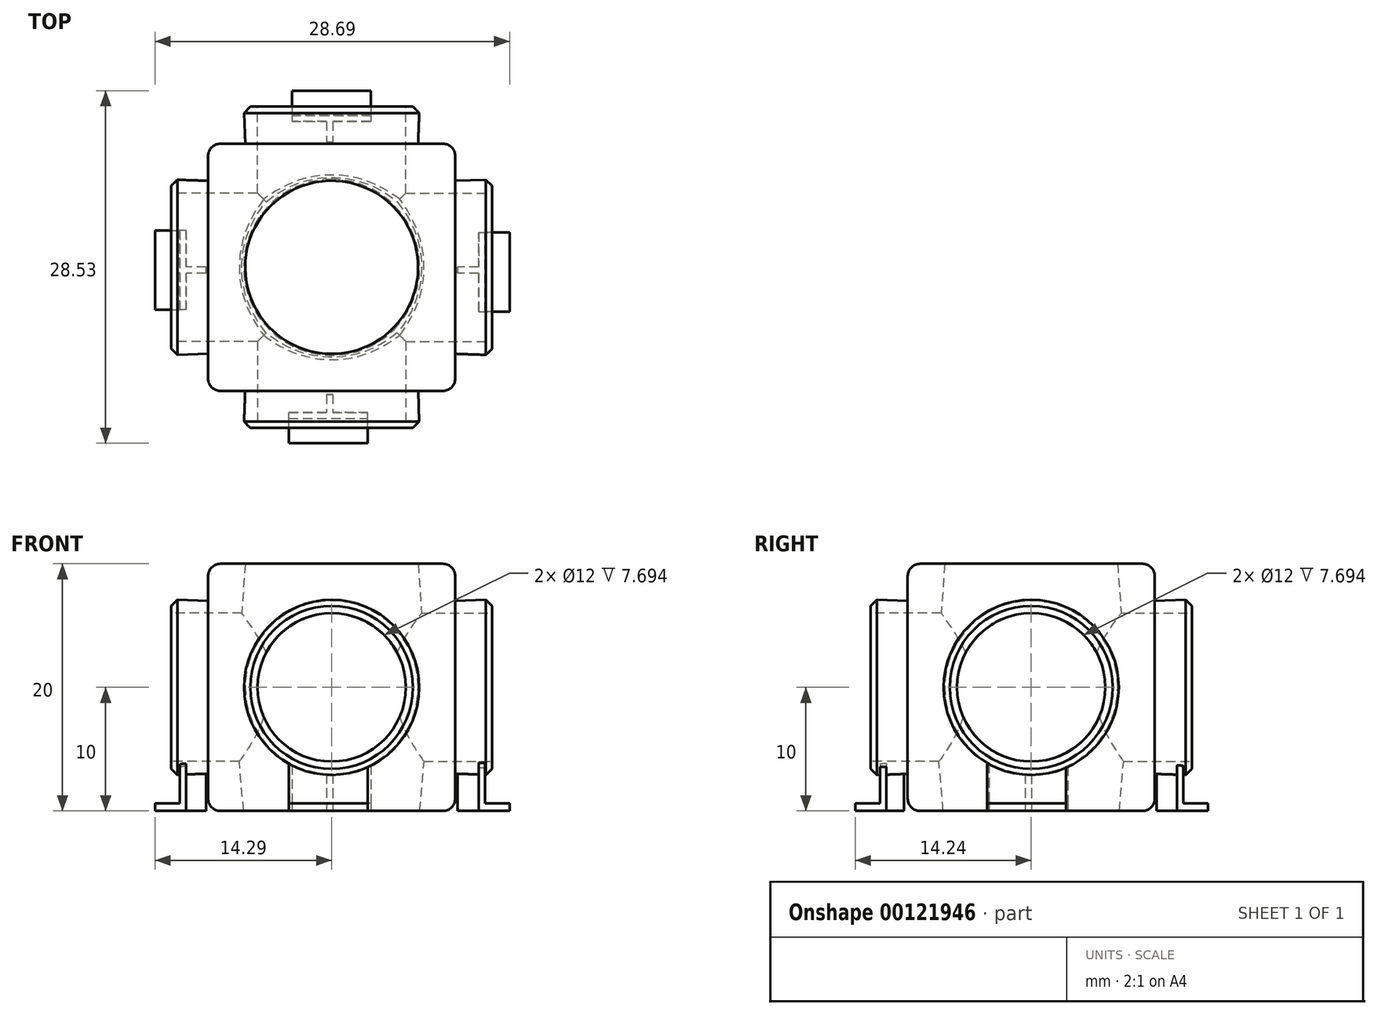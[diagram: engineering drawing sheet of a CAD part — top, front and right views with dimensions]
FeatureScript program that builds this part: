
annotation { "Feature Type Name" : "Feature", "Feature Type Description" : "" }
export const myFeature = defineFeature(function(context is Context, id is Id, definition is map)
    precondition{}
    {
        {
            var Q0;
            Q0=qCreatedBy(makeId("Top.planeOp"),FACE);
            var sketch = newSketch(context, id + "F0", { "sketchPlane" : qUnion([Q0])});
            skLineSegment(sketch, "E0.bottom", {"start": v(0, 0) * mm, "end": v(20, 0) * mm});
            skLineSegment(sketch, "E0.top", {"start": v(0, 20) * mm, "end": v(20, 20) * mm});
            skLineSegment(sketch, "E0.left", {"start": v(0, 0) * mm, "end": v(0, 20) * mm});
            skLineSegment(sketch, "E0.right", {"start": v(20, 0) * mm, "end": v(20, 20) * mm});
            skSolve(sketch);
        }
        {
            var Q0;
            Q0=makeQuery(id+"F0.imprint","IMPRINT",FACE,{"disambiguationData":[TD([[makeQuery(id+"F0.imprint","IMPRINT",EDGE,{"derivedFrom":sQuery(id+"F0.wireOp",EDGE,"E0.bottom")}),1.0]])]});
            extrude(context, id + "F1", {"entities" : qUnion([Q0]), "depth" : 20 * mm});
        }
        {
            var Q0;
            Q0=makeQuery(id+"F1.opExtrude","CAP_FACE",FACE,{"disambiguationData":[OSD([sQuery(id+"F0.wireOp",EDGE,"E0.bottom"),sQuery(id+"F0.wireOp",EDGE,"E0.top"),sQuery(id+"F0.wireOp",EDGE,"E0.left"),sQuery(id+"F0.wireOp",EDGE,"E0.right")])],"isStart":false});
            var sketch = newSketch(context, id + "F2", { "sketchPlane" : qUnion([Q0])});
            skPoint(sketch, "E1", {"position": v(10, 20) * mm});
            skPoint(sketch, "E2", {"position": v(20, 10) * mm});
            skCircle(sketch, "E3", {"center": v(10, 10) * mm, "radius": 7 * mm});
            skSolve(sketch);
        }
        {
            var Q0;
            Q0=makeQuery(id+"F2.imprint","IMPRINT",FACE,{"disambiguationData":[TD([[makeQuery(id+"F2.imprint","IMPRINT",EDGE,{"derivedFrom":sQuery(id+"F2.wireOp",EDGE,"E3")}),1.0]])]});
            extrude(context, id + "F3", {"entities" : qUnion([Q0]), "operationType" : NewBodyOperationType.ADD, "depth" : 3 * mm, "hasDraft" : true, "draftAngle" : 2 * degree});
        }
        {
            var Q0;
            Q0=makeQuery(id+"F1.opExtrude","SWEPT_FACE",FACE,{"disambiguationData":[OSD([sQuery(id+"F0.wireOp",EDGE,"E0.right")])]});
            var sketch = newSketch(context, id + "F4", { "sketchPlane" : qUnion([Q0])});
            skPoint(sketch, "E4", {"position": v(10, 20) * mm});
            skPoint(sketch, "E5", {"position": v(20, 10) * mm});
            skCircle(sketch, "E6", {"center": v(10, 10) * mm, "radius": 7 * mm});
            skSolve(sketch);
        }
        {
            var Q0;
            Q0=makeQuery(id+"F4.imprint","IMPRINT",FACE,{"disambiguationData":[TD([[makeQuery(id+"F4.imprint","IMPRINT",EDGE,{"derivedFrom":sQuery(id+"F4.wireOp",EDGE,"E6")}),1.0]])]});
            extrude(context, id + "F5", {"entities" : qUnion([Q0]), "operationType" : NewBodyOperationType.ADD, "depth" : 3 * mm, "hasDraft" : true, "draftAngle" : 2 * degree});
        }
        {
            var Q0;
            Q0=makeQuery(id+"F1.opExtrude","SWEPT_FACE",FACE,{"disambiguationData":[OSD([sQuery(id+"F0.wireOp",EDGE,"E0.top")])]});
            var sketch = newSketch(context, id + "F6", { "sketchPlane" : qUnion([Q0])});
            skPoint(sketch, "E7", {"position": v(-10, 20) * mm});
            skPoint(sketch, "E8", {"position": v(0, 10) * mm});
            skCircle(sketch, "E9", {"center": v(-10, 10) * mm, "radius": 7.12 * mm});
            skSolve(sketch);
        }
        {
            var Q0;
            Q0=makeQuery(id+"F6.imprint","IMPRINT",FACE,{"disambiguationData":[TD([[makeQuery(id+"F6.imprint","IMPRINT",EDGE,{"derivedFrom":sQuery(id+"F6.wireOp",EDGE,"E9")}),1.0]])]});
            extrude(context, id + "F7", {"entities" : qUnion([Q0]), "operationType" : NewBodyOperationType.REMOVE, "oppositeDirection" : true, "depth" : 10 * mm, "hasDraft" : true, "draftAngle" : 5 * degree});
        }
        {
            var Q0;
            Q0=makeQuery(id+"F1.opExtrude","SWEPT_FACE",FACE,{"disambiguationData":[OSD([sQuery(id+"F0.wireOp",EDGE,"E0.left")])]});
            var sketch = newSketch(context, id + "F8", { "sketchPlane" : qUnion([Q0])});
            skPoint(sketch, "E10", {"position": v(-10, 20) * mm});
            skPoint(sketch, "E11", {"position": v(0, 10) * mm});
            skCircle(sketch, "E12", {"center": v(-10, 10) * mm, "radius": 7 * mm});
            skSolve(sketch);
        }
        {
            var Q0;
            Q0=makeQuery(id+"F8.imprint","IMPRINT",FACE,{"disambiguationData":[TD([[makeQuery(id+"F8.imprint","IMPRINT",EDGE,{"derivedFrom":sQuery(id+"F8.wireOp",EDGE,"E12")}),1.0]])]});
            extrude(context, id + "F9", {"entities" : qUnion([Q0]), "operationType" : NewBodyOperationType.ADD, "depth" : 3 * mm, "hasDraft" : true, "draftAngle" : 2 * degree});
        }
        {
            var Q0;
            Q0=makeQuery(id+"F1.opExtrude","CAP_FACE",FACE,{"disambiguationData":[OSD([sQuery(id+"F0.wireOp",EDGE,"E0.bottom"),sQuery(id+"F0.wireOp",EDGE,"E0.top"),sQuery(id+"F0.wireOp",EDGE,"E0.left"),sQuery(id+"F0.wireOp",EDGE,"E0.right")])],"isStart":true});
            var sketch = newSketch(context, id + "F10", { "sketchPlane" : qUnion([Q0])});
            skPoint(sketch, "E13", {"position": v(10, 0) * mm});
            skPoint(sketch, "E14", {"position": v(20, -10) * mm});
            skCircle(sketch, "E15", {"center": v(10, -10) * mm, "radius": 7 * mm});
            skSolve(sketch);
        }
        {
            var Q0;
            Q0=makeQuery(id+"F10.imprint","IMPRINT",FACE,{"disambiguationData":[TD([[makeQuery(id+"F10.imprint","IMPRINT",EDGE,{"derivedFrom":sQuery(id+"F10.wireOp",EDGE,"E15")}),1.0]])]});
            extrude(context, id + "F11", {"entities" : qUnion([Q0]), "operationType" : NewBodyOperationType.ADD, "depth" : 3 * mm, "hasDraft" : true, "draftAngle" : 2 * degree});
        }
        {
            var Q0;
            Q0=makeQuery(id+"F1.opExtrude","SWEPT_FACE",FACE,{"disambiguationData":[OSD([sQuery(id+"F0.wireOp",EDGE,"E0.bottom")])]});
            var sketch = newSketch(context, id + "F12", { "sketchPlane" : qUnion([Q0])});
            skPoint(sketch, "E16", {"position": v(10, 20) * mm});
            skPoint(sketch, "E17", {"position": v(20, 10) * mm});
            skCircle(sketch, "E18", {"center": v(10, 10) * mm, "radius": 7 * mm});
            skSolve(sketch);
        }
        {
            var Q0;
            Q0=makeQuery(id+"F12.imprint","IMPRINT",FACE,{"disambiguationData":[TD([[makeQuery(id+"F12.imprint","IMPRINT",EDGE,{"derivedFrom":sQuery(id+"F12.wireOp",EDGE,"E18")}),1.0]])]});
            extrude(context, id + "F13", {"entities" : qUnion([Q0]), "operationType" : NewBodyOperationType.REMOVE, "oppositeDirection" : true, "depth" : 10 * mm, "hasDraft" : true, "draftAngle" : 4 * degree});
        }
        {
            var Q0;
            Q0=makeQuery(id+"F3.opExtrude","CAP_FACE",FACE,{"disambiguationData":[OSD([sQuery(id+"F2.wireOp",EDGE,"E3")])],"isStart":false});
            var sketch = newSketch(context, id + "F14", { "sketchPlane" : qUnion([Q0])});
            skCircle(sketch, "E19", {"center": v(10, 10) * mm, "radius": 6 * mm});
            skSolve(sketch);
        }
        {
            var Q0;
            Q0=makeQuery(id+"F9.opExtrude","CAP_FACE",FACE,{"disambiguationData":[OSD([sQuery(id+"F8.wireOp",EDGE,"E12")])],"isStart":false});
            var sketch = newSketch(context, id + "F15", { "sketchPlane" : qUnion([Q0])});
            skCircle(sketch, "E20", {"center": v(-10, 10) * mm, "radius": 6 * mm});
            skSolve(sketch);
        }
        {
            var Q0;
            Q0=makeQuery(id+"F11.opExtrude","CAP_FACE",FACE,{"disambiguationData":[OSD([sQuery(id+"F10.wireOp",EDGE,"E15")])],"isStart":false});
            var sketch = newSketch(context, id + "F16", { "sketchPlane" : qUnion([Q0])});
            skCircle(sketch, "E21", {"center": v(10, -10) * mm, "radius": 6 * mm});
            skSolve(sketch);
        }
        {
            var Q0;
            Q0=makeQuery(id+"F5.opExtrude","CAP_FACE",FACE,{"disambiguationData":[OSD([sQuery(id+"F4.wireOp",EDGE,"E6")])],"isStart":false});
            var sketch = newSketch(context, id + "F17", { "sketchPlane" : qUnion([Q0])});
            skCircle(sketch, "E22", {"center": v(10, 10) * mm, "radius": 6 * mm});
            skSolve(sketch);
        }
        {
            var Q0;
            Q0=makeQuery(id+"F1.opExtrude","SWEPT_EDGE",EDGE,{"disambiguationData":[OSD([sQuery(id+"F0.wireOp",EDGE,"E0.bottom"),sQuery(id+"F0.wireOp",EDGE,"E0.right")])]});
            var Q1;
            Q1=makeQuery(id+"F1.opExtrude","CAP_EDGE",EDGE,{"disambiguationData":[OSD([sQuery(id+"F0.wireOp",EDGE,"E0.right")])],"isStart":false});
            var Q2;
            Q2=makeQuery(id+"F1.opExtrude","CAP_EDGE",EDGE,{"disambiguationData":[OSD([sQuery(id+"F0.wireOp",EDGE,"E0.bottom")])],"isStart":false});
            var Q3;
            Q3=makeQuery(id+"F1.opExtrude","CAP_EDGE",EDGE,{"disambiguationData":[OSD([sQuery(id+"F0.wireOp",EDGE,"E0.bottom")])],"isStart":true});
            var Q4;
            Q4=makeQuery(id+"F1.opExtrude","CAP_EDGE",EDGE,{"disambiguationData":[OSD([sQuery(id+"F0.wireOp",EDGE,"E0.right")])],"isStart":true});
            var Q5;
            Q5=makeQuery(id+"F1.opExtrude","CAP_EDGE",EDGE,{"disambiguationData":[OSD([sQuery(id+"F0.wireOp",EDGE,"E0.top")])],"isStart":true});
            var Q6;
            Q6=makeQuery(id+"F1.opExtrude","CAP_EDGE",EDGE,{"disambiguationData":[OSD([sQuery(id+"F0.wireOp",EDGE,"E0.left")])],"isStart":true});
            var Q7;
            Q7=makeQuery(id+"F1.opExtrude","SWEPT_EDGE",EDGE,{"disambiguationData":[OSD([sQuery(id+"F0.wireOp",EDGE,"E0.bottom"),sQuery(id+"F0.wireOp",EDGE,"E0.left")])]});
            var Q8;
            Q8=makeQuery(id+"F1.opExtrude","SWEPT_EDGE",EDGE,{"disambiguationData":[OSD([sQuery(id+"F0.wireOp",EDGE,"E0.top"),sQuery(id+"F0.wireOp",EDGE,"E0.left")])]});
            var Q9;
            Q9=makeQuery(id+"F1.opExtrude","CAP_EDGE",EDGE,{"disambiguationData":[OSD([sQuery(id+"F0.wireOp",EDGE,"E0.left")])],"isStart":false});
            var Q10;
            Q10=makeQuery(id+"F1.opExtrude","SWEPT_EDGE",EDGE,{"disambiguationData":[OSD([sQuery(id+"F0.wireOp",EDGE,"E0.top"),sQuery(id+"F0.wireOp",EDGE,"E0.right")])]});
            var Q11;
            Q11=makeQuery(id+"F1.opExtrude","CAP_EDGE",EDGE,{"disambiguationData":[OSD([sQuery(id+"F0.wireOp",EDGE,"E0.top")])],"isStart":false});
            fillet(context, id + "F18", {"entities" : qUnion([Q0, Q1, Q2, Q3, Q4, Q5, Q6, Q7, Q8, Q9, Q10, Q11]), "radius" : 1 * mm, "tangentPropagation" : true, "allowEdgeOverflow" : false});
        }
        {
            var Q0;
            Q0=makeQuery(id+"F17.imprint","IMPRINT",FACE,{"disambiguationData":[TD([[makeQuery(id+"F17.imprint","IMPRINT",EDGE,{"derivedFrom":sQuery(id+"F17.wireOp",EDGE,"E22")}),1.0]])]});
            extrude(context, id + "F19", {"entities" : qUnion([Q0]), "operationType" : NewBodyOperationType.REMOVE, "oppositeDirection" : true, "depth" : 12 * mm});
        }
        {
            var Q0;
            Q0=makeQuery(id+"F16.imprint","IMPRINT",FACE,{"disambiguationData":[TD([[makeQuery(id+"F16.imprint","IMPRINT",EDGE,{"derivedFrom":sQuery(id+"F16.wireOp",EDGE,"E21")}),1.0]])]});
            extrude(context, id + "F20", {"entities" : qUnion([Q0]), "operationType" : NewBodyOperationType.REMOVE, "oppositeDirection" : true, "depth" : 12 * mm});
        }
        {
            var Q0;
            Q0=makeQuery(id+"F15.imprint","IMPRINT",FACE,{"disambiguationData":[TD([[makeQuery(id+"F15.imprint","IMPRINT",EDGE,{"derivedFrom":sQuery(id+"F15.wireOp",EDGE,"E20")}),1.0]])]});
            extrude(context, id + "F21", {"entities" : qUnion([Q0]), "operationType" : NewBodyOperationType.REMOVE, "oppositeDirection" : true, "depth" : 12 * mm});
        }
        {
            var Q0;
            Q0=makeQuery(id+"F14.imprint","IMPRINT",FACE,{"disambiguationData":[TD([[makeQuery(id+"F14.imprint","IMPRINT",EDGE,{"derivedFrom":sQuery(id+"F14.wireOp",EDGE,"E19")}),1.0]])]});
            extrude(context, id + "F22", {"entities" : qUnion([Q0]), "operationType" : NewBodyOperationType.REMOVE, "oppositeDirection" : true, "depth" : 12 * mm});
        }
        {
            var Q0;
            Q0=makeQuery(id+"F13.opExtrude","CAP_EDGE",EDGE,{"disambiguationData":[OSD([sQuery(id+"F12.wireOp",EDGE,"E18")])],"isStart":false});
            var Q1;
            Q1=makeQuery(id+"F11.boolean.opBoolean","COPY",EDGE,{"derivedFrom":makeQuery(id+"F11.opExtrude","CAP_EDGE",EDGE,{"disambiguationData":[OSD([sQuery(id+"F10.wireOp",EDGE,"E15")])],"isStart":true})});
            var Q2;
            Q2=makeQuery(id+"F9.boolean.opBoolean","COPY",EDGE,{"derivedFrom":makeQuery(id+"F9.opExtrude","CAP_EDGE",EDGE,{"disambiguationData":[OSD([sQuery(id+"F8.wireOp",EDGE,"E12")])],"isStart":true})});
            var Q3;
            Q3=makeQuery(id+"F3.boolean.opBoolean","COPY",EDGE,{"derivedFrom":makeQuery(id+"F3.opExtrude","CAP_EDGE",EDGE,{"disambiguationData":[OSD([sQuery(id+"F2.wireOp",EDGE,"E3")])],"isStart":true})});
            var Q4;
            Q4=makeQuery(id+"F5.boolean.opBoolean","COPY",EDGE,{"derivedFrom":makeQuery(id+"F5.opExtrude","CAP_EDGE",EDGE,{"disambiguationData":[OSD([sQuery(id+"F4.wireOp",EDGE,"E6")])],"isStart":true})});
            var Q5;
            Q5=makeQuery(id+"F7.boolean.opBoolean","COPY",EDGE,{"derivedFrom":makeQuery(id+"F7.opExtrude","CAP_EDGE",EDGE,{"disambiguationData":[OSD([sQuery(id+"F6.wireOp",EDGE,"E9")])],"isStart":true})});
            var Q6;
            Q6=makeQuery(id+"F9.opExtrude","CAP_EDGE",EDGE,{"disambiguationData":[OSD([sQuery(id+"F8.wireOp",EDGE,"E12")])],"isStart":false});
            var Q7;
            Q7=makeQuery(id+"F11.opExtrude","CAP_EDGE",EDGE,{"disambiguationData":[OSD([sQuery(id+"F10.wireOp",EDGE,"E15")])],"isStart":false});
            var Q8;
            Q8=makeQuery(id+"F5.opExtrude","CAP_EDGE",EDGE,{"disambiguationData":[OSD([sQuery(id+"F4.wireOp",EDGE,"E6")])],"isStart":false});
            var Q9;
            Q9=makeQuery(id+"F3.opExtrude","CAP_EDGE",EDGE,{"disambiguationData":[OSD([sQuery(id+"F2.wireOp",EDGE,"E3")])],"isStart":false});
            var Q10;
            Q10=makeQuery(id+"F13.boolean.opBoolean","COPY",EDGE,{"derivedFrom":makeQuery(id+"F13.opExtrude","CAP_EDGE",EDGE,{"disambiguationData":[OSD([sQuery(id+"F12.wireOp",EDGE,"E18")])],"isStart":true})});
            chamfer(context, id + "F23", {"entities" : qUnion([Q0, Q1, Q2, Q3, Q4, Q5, Q6, Q7, Q8, Q9, Q10]), "width" : 0.5 * mm, "tangentPropagation" : true});
        }
        {
            var Q0;
            Q0=makeQuery(id+"F1.opExtrude","SWEPT_FACE",FACE,{"disambiguationData":[OSD([sQuery(id+"F0.wireOp",EDGE,"E0.top")])]});
            var sketch = newSketch(context, id + "F24", { "sketchPlane" : qUnion([Q0])});
            skLineSegment(sketch, "E23.bottom", {"start": v(-10.08, 22.3) * mm, "end": v(-9.58, 22.3) * mm});
            skLineSegment(sketch, "E23.top", {"start": v(-10.08, -2.24) * mm, "end": v(-9.58, -2.24) * mm});
            skLineSegment(sketch, "E23.left", {"start": v(-10.08, 22.3) * mm, "end": v(-10.08, -2.24) * mm});
            skLineSegment(sketch, "E23.right", {"start": v(-9.58, 22.3) * mm, "end": v(-9.58, -2.24) * mm});
            skLineSegment(sketch, "E24.bottom", {"start": v(-22.4, 10.02) * mm, "end": v(2.29, 10.02) * mm});
            skLineSegment(sketch, "E24.top", {"start": v(-22.4, 9.52) * mm, "end": v(2.29, 9.52) * mm});
            skLineSegment(sketch, "E24.left", {"start": v(-22.4, 10.02) * mm, "end": v(-22.4, 9.52) * mm});
            skLineSegment(sketch, "E24.right", {"start": v(2.29, 10.02) * mm, "end": v(2.29, 9.52) * mm});
            skLineSegment(sketch, "E25.bottom", {"start": v(-21.9, 12.82) * mm, "end": v(-22.4, 12.82) * mm});
            skLineSegment(sketch, "E25.top", {"start": v(-21.9, 6.42) * mm, "end": v(-22.4, 6.42) * mm});
            skLineSegment(sketch, "E25.left", {"start": v(-21.9, 12.82) * mm, "end": v(-21.9, 6.42) * mm});
            skLineSegment(sketch, "E25.right", {"start": v(-22.4, 12.82) * mm, "end": v(-22.4, 6.42) * mm});
            skLineSegment(sketch, "E26.bottom", {"start": v(1.79, 12.98) * mm, "end": v(2.29, 12.98) * mm});
            skLineSegment(sketch, "E26.top", {"start": v(1.79, 6.58) * mm, "end": v(2.29, 6.58) * mm});
            skLineSegment(sketch, "E26.left", {"start": v(1.79, 12.98) * mm, "end": v(1.79, 6.58) * mm});
            skLineSegment(sketch, "E26.right", {"start": v(2.29, 12.98) * mm, "end": v(2.29, 6.58) * mm});
            skLineSegment(sketch, "E27.bottom", {"start": v(-13.18, 22.3) * mm, "end": v(-6.78, 22.3) * mm});
            skLineSegment(sketch, "E27.top", {"start": v(-13.18, 21.8) * mm, "end": v(-6.78, 21.8) * mm});
            skLineSegment(sketch, "E27.left", {"start": v(-13.18, 22.3) * mm, "end": v(-13.18, 21.8) * mm});
            skLineSegment(sketch, "E27.right", {"start": v(-6.78, 22.3) * mm, "end": v(-6.78, 21.8) * mm});
            skLineSegment(sketch, "E28.bottom", {"start": v(-12.93, -2.24) * mm, "end": v(-6.53, -2.24) * mm});
            skLineSegment(sketch, "E28.top", {"start": v(-12.93, -1.74) * mm, "end": v(-6.53, -1.74) * mm});
            skLineSegment(sketch, "E28.left", {"start": v(-12.93, -2.24) * mm, "end": v(-12.93, -1.74) * mm});
            skLineSegment(sketch, "E28.right", {"start": v(-6.53, -2.24) * mm, "end": v(-6.53, -1.74) * mm});
            skLineSegment(sketch, "E29.bottom", {"start": v(-20.19, 20.14) * mm, "end": v(0.17, 20.14) * mm});
            skLineSegment(sketch, "E29.top", {"start": v(-20.19, -0.3) * mm, "end": v(0.17, -0.3) * mm});
            skLineSegment(sketch, "E29.left", {"start": v(-20.19, 20.14) * mm, "end": v(-20.19, -0.3) * mm});
            skLineSegment(sketch, "E29.right", {"start": v(0.17, 20.14) * mm, "end": v(0.17, -0.3) * mm});
            skSolve(sketch);
        }
        {
            var Q0;
            {var subQ5=sQuery(id+"F24.wireOp",EDGE,"E27.left");Q0=makeQuery(id+"F24.imprint","IMPRINT",FACE,{"disambiguationData":[TD([[makeQuery(id+"F24.imprint","IMPRINT",EDGE,{"derivedFrom":subQ5}),1.0]])]});}
            var Q1;
            {var subQ0=sQuery(id+"F24.wireOp",EDGE,"E27.bottom");var subQ1=sQuery(id+"F24.wireOp",EDGE,"E23.left");var subQ2=makeQuery(id+"F24.imprint","INTERSECT",VERTEX,{"derivedFrom":[subQ1,subQ0]});Q1=makeQuery(id+"F24.imprint","IMPRINT",FACE,{"disambiguationData":[TD([[makeQuery(id+"F24.imprint","IMPRINT",EDGE,{"disambiguationData":[TD([[subQ2,-1.0]])],"derivedFrom":subQ1}),1.0]])]});}
            var Q2;
            {var subQ5=sQuery(id+"F24.wireOp",EDGE,"E27.right");Q2=makeQuery(id+"F24.imprint","IMPRINT",FACE,{"disambiguationData":[TD([[makeQuery(id+"F24.imprint","IMPRINT",EDGE,{"derivedFrom":subQ5}),-1.0]])]});}
            var Q3;
            {var subQ0=sQuery(id+"F24.wireOp",EDGE,"E27.top");var subQ1=sQuery(id+"F24.wireOp",EDGE,"E23.left");var subQ2=makeQuery(id+"F24.imprint","INTERSECT",VERTEX,{"derivedFrom":[subQ1,subQ0]});Q3=makeQuery(id+"F24.imprint","IMPRINT",FACE,{"disambiguationData":[TD([[makeQuery(id+"F24.imprint","IMPRINT",EDGE,{"disambiguationData":[TD([[subQ2,-1.0]])],"derivedFrom":subQ1}),1.0]])]});}
            var Q4;
            {var subQ5=sQuery(id+"F24.wireOp",EDGE,"E26.bottom");Q4=makeQuery(id+"F24.imprint","IMPRINT",FACE,{"disambiguationData":[TD([[makeQuery(id+"F24.imprint","IMPRINT",EDGE,{"derivedFrom":subQ5}),-1.0]])]});}
            var Q5;
            {var subQ0=sQuery(id+"F24.wireOp",EDGE,"E26.right");var subQ1=sQuery(id+"F24.wireOp",EDGE,"E24.bottom");var subQ2=makeQuery(id+"F24.imprint","INTERSECT",VERTEX,{"derivedFrom":[subQ1,subQ0]});Q5=makeQuery(id+"F24.imprint","IMPRINT",FACE,{"disambiguationData":[TD([[makeQuery(id+"F24.imprint","IMPRINT",EDGE,{"disambiguationData":[TD([[subQ2,1.0]])],"derivedFrom":subQ1}),-1.0]])]});}
            var Q6;
            {var subQ5=sQuery(id+"F24.wireOp",EDGE,"E26.top");Q6=makeQuery(id+"F24.imprint","IMPRINT",FACE,{"disambiguationData":[TD([[makeQuery(id+"F24.imprint","IMPRINT",EDGE,{"derivedFrom":subQ5}),1.0]])]});}
            var Q7;
            {var subQ0=sQuery(id+"F24.wireOp",EDGE,"E29.right");var subQ1=sQuery(id+"F24.wireOp",EDGE,"E24.bottom");var subQ2=makeQuery(id+"F24.imprint","INTERSECT",VERTEX,{"derivedFrom":[subQ1,subQ0]});Q7=makeQuery(id+"F24.imprint","IMPRINT",FACE,{"disambiguationData":[TD([[makeQuery(id+"F24.imprint","IMPRINT",EDGE,{"disambiguationData":[TD([[subQ2,-1.0]])],"derivedFrom":subQ1}),-1.0]])]});}
            var Q8;
            {var subQ5=sQuery(id+"F24.wireOp",EDGE,"E25.bottom");Q8=makeQuery(id+"F24.imprint","IMPRINT",FACE,{"disambiguationData":[TD([[makeQuery(id+"F24.imprint","IMPRINT",EDGE,{"derivedFrom":subQ5}),1.0]])]});}
            var Q9;
            {var subQ0=sQuery(id+"F24.wireOp",EDGE,"E25.right");var subQ1=sQuery(id+"F24.wireOp",EDGE,"E24.bottom");var subQ2=makeQuery(id+"F24.imprint","INTERSECT",VERTEX,{"derivedFrom":[subQ1,subQ0]});Q9=makeQuery(id+"F24.imprint","IMPRINT",FACE,{"disambiguationData":[TD([[makeQuery(id+"F24.imprint","IMPRINT",EDGE,{"disambiguationData":[TD([[subQ2,-1.0]])],"derivedFrom":subQ1}),-1.0]])]});}
            var Q10;
            {var subQ5=sQuery(id+"F24.wireOp",EDGE,"E25.top");Q10=makeQuery(id+"F24.imprint","IMPRINT",FACE,{"disambiguationData":[TD([[makeQuery(id+"F24.imprint","IMPRINT",EDGE,{"derivedFrom":subQ5}),-1.0]])]});}
            var Q11;
            {var subQ0=sQuery(id+"F24.wireOp",EDGE,"E25.left");var subQ1=sQuery(id+"F24.wireOp",EDGE,"E24.bottom");var subQ2=makeQuery(id+"F24.imprint","INTERSECT",VERTEX,{"derivedFrom":[subQ1,subQ0]});Q11=makeQuery(id+"F24.imprint","IMPRINT",FACE,{"disambiguationData":[TD([[makeQuery(id+"F24.imprint","IMPRINT",EDGE,{"disambiguationData":[TD([[subQ2,-1.0]])],"derivedFrom":subQ1}),-1.0]])]});}
            var Q12;
            {var subQ5=sQuery(id+"F24.wireOp",EDGE,"E28.left");Q12=makeQuery(id+"F24.imprint","IMPRINT",FACE,{"disambiguationData":[TD([[makeQuery(id+"F24.imprint","IMPRINT",EDGE,{"derivedFrom":subQ5}),-1.0]])]});}
            var Q13;
            {var subQ0=sQuery(id+"F24.wireOp",EDGE,"E28.bottom");var subQ1=sQuery(id+"F24.wireOp",EDGE,"E23.left");var subQ2=makeQuery(id+"F24.imprint","INTERSECT",VERTEX,{"derivedFrom":[subQ1,subQ0]});Q13=makeQuery(id+"F24.imprint","IMPRINT",FACE,{"disambiguationData":[TD([[makeQuery(id+"F24.imprint","IMPRINT",EDGE,{"disambiguationData":[TD([[subQ2,1.0]])],"derivedFrom":subQ1}),1.0]])]});}
            var Q14;
            {var subQ5=sQuery(id+"F24.wireOp",EDGE,"E28.right");Q14=makeQuery(id+"F24.imprint","IMPRINT",FACE,{"disambiguationData":[TD([[makeQuery(id+"F24.imprint","IMPRINT",EDGE,{"derivedFrom":subQ5}),1.0]])]});}
            var Q15;
            {var subQ0=sQuery(id+"F24.wireOp",EDGE,"E29.top");var subQ1=sQuery(id+"F24.wireOp",EDGE,"E23.left");var subQ2=makeQuery(id+"F24.imprint","INTERSECT",VERTEX,{"derivedFrom":[subQ1,subQ0]});Q15=makeQuery(id+"F24.imprint","IMPRINT",FACE,{"disambiguationData":[TD([[makeQuery(id+"F24.imprint","IMPRINT",EDGE,{"disambiguationData":[TD([[subQ2,-1.0]])],"derivedFrom":subQ1}),1.0]])]});}
            extrude(context, id + "F25", {"entities" : qUnion([Q0, Q1, Q2, Q3, Q4, Q5, Q6, Q7, Q8, Q9, Q10, Q11, Q12, Q13, Q14, Q15]), "operationType" : NewBodyOperationType.ADD, "endBound" : BoundingType.UP_TO_NEXT, "oppositeDirection" : true, "depth" : 25 * mm});
        }
        {
            var Q0;
            Q0=makeQuery(id+"F25.opExtrude","SWEPT_FACE",FACE,{"disambiguationData":[OSD([sQuery(id+"F24.wireOp",EDGE,"E27.bottom")])]});
            var sketch = newSketch(context, id + "F26", { "sketchPlane" : qUnion([Q0])});
            skLineSegment(sketch, "E30.bottom", {"start": v(13.18, 20) * mm, "end": v(6.78, 20) * mm});
            skLineSegment(sketch, "E30.top", {"start": v(13.18, 19.4) * mm, "end": v(6.78, 19.4) * mm});
            skLineSegment(sketch, "E30.left", {"start": v(13.18, 20) * mm, "end": v(13.18, 19.4) * mm});
            skLineSegment(sketch, "E30.right", {"start": v(6.78, 20) * mm, "end": v(6.78, 19.4) * mm});
            skSolve(sketch);
        }
        {
            var Q0;
            Q0=makeQuery(id+"F26.imprint","IMPRINT",FACE,{"disambiguationData":[TD([[makeQuery(id+"F26.imprint","IMPRINT",EDGE,{"derivedFrom":sQuery(id+"F26.wireOp",EDGE,"E30.bottom")}),1.0]])]});
            extrude(context, id + "F27", {"entities" : qUnion([Q0]), "operationType" : NewBodyOperationType.ADD, "depth" : 2 * mm});
        }
        {
            var Q0;
            Q0=makeQuery(id+"F25.opExtrude","SWEPT_FACE",FACE,{"disambiguationData":[OSD([sQuery(id+"F24.wireOp",EDGE,"E25.right")])]});
            var sketch = newSketch(context, id + "F28", { "sketchPlane" : qUnion([Q0])});
            skLineSegment(sketch, "E31.bottom", {"start": v(20, 6.42) * mm, "end": v(19.4, 6.42) * mm});
            skLineSegment(sketch, "E31.top", {"start": v(20, 12.82) * mm, "end": v(19.4, 12.82) * mm});
            skLineSegment(sketch, "E31.left", {"start": v(20, 6.42) * mm, "end": v(20, 12.82) * mm});
            skLineSegment(sketch, "E31.right", {"start": v(19.4, 6.42) * mm, "end": v(19.4, 12.82) * mm});
            skSolve(sketch);
        }
        {
            var Q0;
            Q0=makeQuery(id+"F28.imprint","IMPRINT",FACE,{"disambiguationData":[TD([[makeQuery(id+"F28.imprint","IMPRINT",EDGE,{"derivedFrom":sQuery(id+"F28.wireOp",EDGE,"E31.bottom")}),1.0]])]});
            extrude(context, id + "F29", {"entities" : qUnion([Q0]), "operationType" : NewBodyOperationType.ADD, "depth" : 2 * mm});
        }
        {
            var Q0;
            Q0=makeQuery(id+"F25.opExtrude","SWEPT_FACE",FACE,{"disambiguationData":[OSD([sQuery(id+"F24.wireOp",EDGE,"E28.bottom")])]});
            var sketch = newSketch(context, id + "F30", { "sketchPlane" : qUnion([Q0])});
            skLineSegment(sketch, "E32.bottom", {"start": v(6.53, -20) * mm, "end": v(12.93, -20) * mm});
            skLineSegment(sketch, "E32.top", {"start": v(6.53, -19.4) * mm, "end": v(12.93, -19.4) * mm});
            skLineSegment(sketch, "E32.left", {"start": v(6.53, -20) * mm, "end": v(6.53, -19.4) * mm});
            skLineSegment(sketch, "E32.right", {"start": v(12.93, -20) * mm, "end": v(12.93, -19.4) * mm});
            skSolve(sketch);
        }
        {
            var Q0;
            Q0=makeQuery(id+"F30.imprint","IMPRINT",FACE,{"disambiguationData":[TD([[makeQuery(id+"F30.imprint","IMPRINT",EDGE,{"derivedFrom":sQuery(id+"F30.wireOp",EDGE,"E32.bottom")}),-1.0]])]});
            extrude(context, id + "F31", {"entities" : qUnion([Q0]), "operationType" : NewBodyOperationType.ADD, "depth" : 2 * mm});
        }
        {
            var Q0;
            Q0=makeQuery(id+"F25.opExtrude","SWEPT_FACE",FACE,{"disambiguationData":[OSD([sQuery(id+"F24.wireOp",EDGE,"E26.right")])]});
            var sketch = newSketch(context, id + "F32", { "sketchPlane" : qUnion([Q0])});
            skLineSegment(sketch, "E33.bottom", {"start": v(-20, 12.98) * mm, "end": v(-19.4, 12.98) * mm});
            skLineSegment(sketch, "E33.top", {"start": v(-20, 6.58) * mm, "end": v(-19.4, 6.58) * mm});
            skLineSegment(sketch, "E33.left", {"start": v(-20, 12.98) * mm, "end": v(-20, 6.58) * mm});
            skLineSegment(sketch, "E33.right", {"start": v(-19.4, 12.98) * mm, "end": v(-19.4, 6.58) * mm});
            skSolve(sketch);
        }
        {
            var Q0;
            Q0=makeQuery(id+"F32.imprint","IMPRINT",FACE,{"disambiguationData":[TD([[makeQuery(id+"F32.imprint","IMPRINT",EDGE,{"derivedFrom":sQuery(id+"F32.wireOp",EDGE,"E33.bottom")}),1.0]])]});
            extrude(context, id + "F33", {"entities" : qUnion([Q0]), "operationType" : NewBodyOperationType.ADD, "depth" : 2 * mm});
        }
        {
            var Q0;
            Q0=makeQuery(id+"F1.opExtrude","SWEPT_BODY",BODY,{"disambiguationData":[OSD([sQuery(id+"F0.wireOp",EDGE,"E0.bottom"),sQuery(id+"F0.wireOp",EDGE,"E0.top"),sQuery(id+"F0.wireOp",EDGE,"E0.left"),sQuery(id+"F0.wireOp",EDGE,"E0.right")])]});
            var Q1;
            {var subQ0=sQuery(id+"F0.wireOp",EDGE,"E0.top");Q1=makeQuery(id+"F18.opFillet","BLEND_EDGE",EDGE,{"blendedFrom":[makeQuery(id+"F1.opExtrude","CAP_EDGE",EDGE,{"disambiguationData":[OSD([subQ0])],"isStart":false}),makeQuery(id+"F1.opExtrude","SWEPT_FACE",FACE,{"disambiguationData":[OSD([subQ0])]})],"blendedInto":[makeQuery(id+"F1.opExtrude","SWEPT_FACE",FACE,{"disambiguationData":[OSD([subQ0])]})]});}
            transform(context, id + "F34", {"entities" : qUnion([Q0]), "transformType" : TransformType.ROTATION, "transformAxis" : qUnion([Q1]), "angle" : 90 * degree, "oppositeDirection" : true, "makeCopy" : false});
        }
    });
